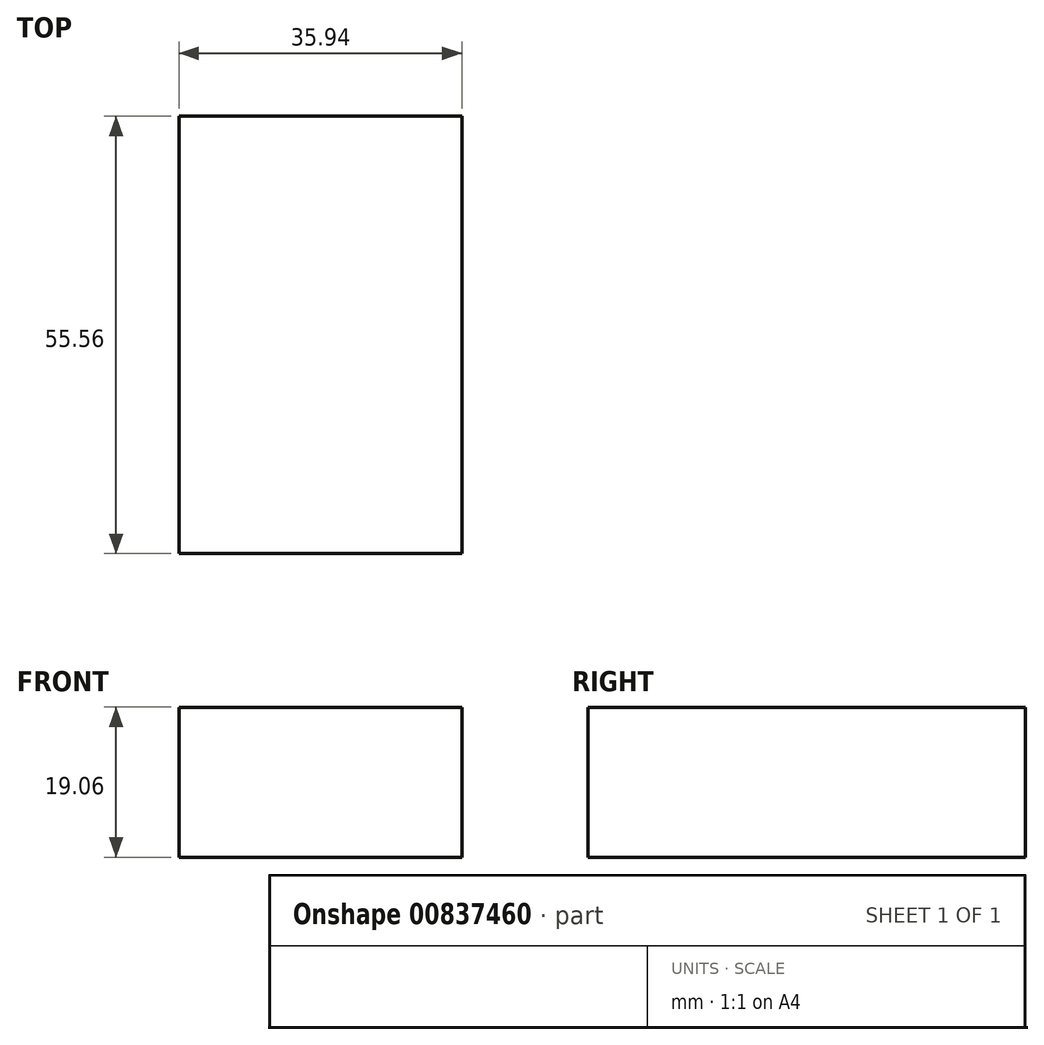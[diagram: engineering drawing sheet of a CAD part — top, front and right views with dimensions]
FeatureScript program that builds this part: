
annotation { "Feature Type Name" : "Feature", "Feature Type Description" : "" }
export const myFeature = defineFeature(function(context is Context, id is Id, definition is map)
    precondition{}
    {
        {
            var Q0;
            Q0=qCreatedBy(makeId("Right.planeOp"),FACE);
            var sketch = newSketch(context, id + "F0", { "sketchPlane" : qUnion([Q0])});
            skLineSegment(sketch, "E0.bottom", {"start": v(27.78, 9.53) * mm, "end": v(-27.78, 9.53) * mm});
            skLineSegment(sketch, "E0.top", {"start": v(27.78, -9.53) * mm, "end": v(-27.78, -9.53) * mm});
            skLineSegment(sketch, "E0.left", {"start": v(27.78, 9.53) * mm, "end": v(27.78, -9.52) * mm});
            skLineSegment(sketch, "E0.right", {"start": v(-27.78, 9.53) * mm, "end": v(-27.78, -9.52) * mm});
            skPoint(sketch, "E0.middle", {"position": v(0, 0) * mm});
            skSolve(sketch);
        }
        {
            var Q0;
            Q0=makeQuery(id+"F0.imprint","IMPRINT",FACE,{"disambiguationData":[TD([[makeQuery(id+"F0.imprint","IMPRINT",EDGE,{"derivedFrom":sQuery(id+"F0.wireOp",EDGE,"E0.bottom")}),1.0]])]});
            extrude(context, id + "F1", {"entities" : qUnion([Q0]), "endBound" : BoundingType.SYMMETRIC, "depth" : ((((69 + 1 / 8) / 2) + 1.38)) * mm, "offsetDistance" : 25.4 * mm});
        }
    });
